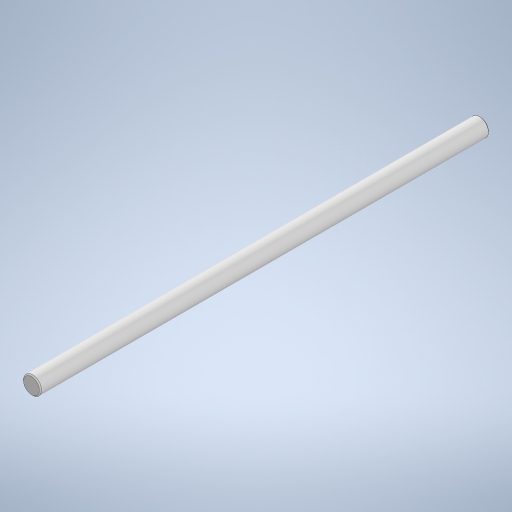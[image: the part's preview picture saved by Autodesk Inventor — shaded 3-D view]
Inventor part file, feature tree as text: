
AUTODESK INVENTOR PART (.ipt)
format: ipt  version: 2024 (Build 280153000, 153)  size: 239,104 bytes
history: native  units: mm
features: extrude x1, chamfer x1, sketch x1
ambient origin geometry x8: Origin, YZ Plane, XZ Plane, XY Plane, X Axis, Y Axis, Z Axis, Center Point
bodies: Solid1 (feature_tree)
feature tree (3):
  extrude  "Extrusion1"  Depth=200.0mm TaperAngle=0.0deg
  chamfer  "Chamfer1"  Distance=0.5mm Angle=45.0deg
  sketch  "Sketch1"  dims[d0=8.0mm d1=200.0mm d2=0.0mm d3=0.5mm d4=2.0mm d5=45.0deg]
